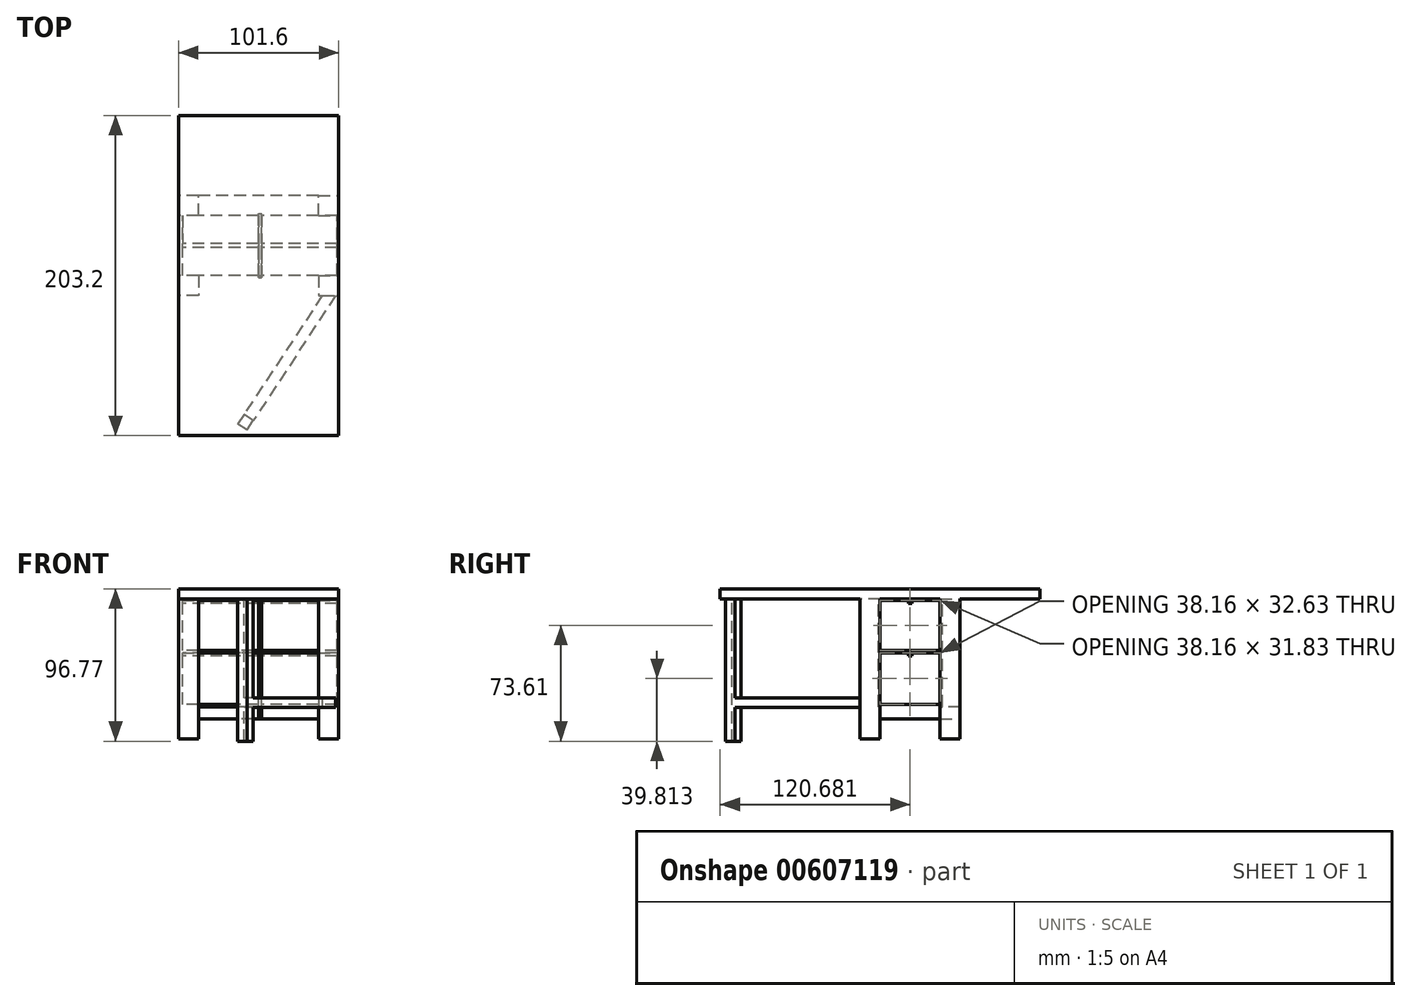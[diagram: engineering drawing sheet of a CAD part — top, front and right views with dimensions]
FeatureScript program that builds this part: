
annotation { "Feature Type Name" : "Feature", "Feature Type Description" : "" }
export const myFeature = defineFeature(function(context is Context, id is Id, definition is map)
    precondition{}
    {
        {
            var Q0;
            Q0=qCreatedBy(makeId("Top.planeOp"),FACE);
            var sketch = newSketch(context, id + "F0", { "sketchPlane" : qUnion([Q0])});
            skLineSegment(sketch, "E0.bottom", {"start": v(-51.6, 50.8) * mm, "end": v(24.6, 50.8) * mm});
            skLineSegment(sketch, "E0.top", {"start": v(-51.6, 12.7) * mm, "end": v(24.6, 12.7) * mm});
            skLineSegment(sketch, "E0.left", {"start": v(-51.6, 50.8) * mm, "end": v(-51.6, 12.7) * mm});
            skLineSegment(sketch, "E0.right", {"start": v(24.6, 50.8) * mm, "end": v(24.6, 12.7) * mm});
            skLineSegment(sketch, "E1.bottom", {"start": v(-51.6, 50.8) * mm, "end": v(-64.3, 50.8) * mm});
            skLineSegment(sketch, "E1.top", {"start": v(-51.6, 63.5) * mm, "end": v(-64.3, 63.5) * mm});
            skLineSegment(sketch, "E1.left", {"start": v(-51.6, 50.8) * mm, "end": v(-51.6, 63.5) * mm});
            skLineSegment(sketch, "E1.right", {"start": v(-64.3, 50.8) * mm, "end": v(-64.3, 63.5) * mm});
            skLineSegment(sketch, "E2.bottom", {"start": v(24.6, 50.8) * mm, "end": v(37.3, 50.8) * mm});
            skLineSegment(sketch, "E2.top", {"start": v(24.6, 63.5) * mm, "end": v(37.3, 63.5) * mm});
            skLineSegment(sketch, "E2.left", {"start": v(24.6, 50.8) * mm, "end": v(24.6, 63.5) * mm});
            skLineSegment(sketch, "E2.right", {"start": v(37.3, 50.8) * mm, "end": v(37.3, 63.5) * mm});
            skLineSegment(sketch, "E3.bottom", {"start": v(24.6, 12.7) * mm, "end": v(37.3, 12.7) * mm});
            skLineSegment(sketch, "E3.top", {"start": v(24.6, 0) * mm, "end": v(37.3, 0) * mm});
            skLineSegment(sketch, "E3.left", {"start": v(24.6, 12.7) * mm, "end": v(24.6, 0) * mm});
            skLineSegment(sketch, "E3.right", {"start": v(37.3, 12.7) * mm, "end": v(37.3, 0) * mm});
            skLineSegment(sketch, "E4.bottom", {"start": v(-51.6, 12.7) * mm, "end": v(-64.3, 12.7) * mm});
            skLineSegment(sketch, "E4.top", {"start": v(-51.6, 0) * mm, "end": v(-64.3, 0) * mm});
            skLineSegment(sketch, "E4.left", {"start": v(-51.6, 12.7) * mm, "end": v(-51.6, 0) * mm});
            skLineSegment(sketch, "E4.right", {"start": v(-64.3, 12.7) * mm, "end": v(-64.3, 0) * mm});
            skLineSegment(sketch, "E5.bottom", {"start": v(-64.3, 50.8) * mm, "end": v(-51.6, 50.8) * mm});
            skLineSegment(sketch, "E5.top", {"start": v(-64.3, 12.7) * mm, "end": v(-51.6, 12.7) * mm});
            skLineSegment(sketch, "E5.left", {"start": v(-64.3, 50.8) * mm, "end": v(-64.3, 12.7) * mm});
            skLineSegment(sketch, "E6.top", {"start": v(-51.6, 0) * mm, "end": v(24.6, 0) * mm});
            skLineSegment(sketch, "E7.right", {"start": v(37.3, 50.8) * mm, "end": v(37.3, 12.7) * mm});
            skLineSegment(sketch, "E8.bottom", {"start": v(24.6, 63.5) * mm, "end": v(-51.6, 63.5) * mm});
            skLineSegment(sketch, "E8.top", {"start": v(24.6, 50.8) * mm, "end": v(-51.6, 50.8) * mm});
            skLineSegment(sketch, "E8.left", {"start": v(24.6, 63.5) * mm, "end": v(24.6, 50.8) * mm});
            skLineSegment(sketch, "E8.right", {"start": v(-51.6, 63.5) * mm, "end": v(-51.6, 50.8) * mm});
            skSolve(sketch);
        }
        {
            var Q0;
            Q0=makeQuery(id+"F0.imprint","IMPRINT",FACE,{"disambiguationData":[TD([[makeQuery(id+"F0.imprint","IMPRINT",EDGE,{"derivedFrom":sQuery(id+"F0.wireOp",EDGE,"E1.top")}),1.0]])]});
            var Q1;
            Q1=makeQuery(id+"F0.imprint","IMPRINT",FACE,{"disambiguationData":[TD([[makeQuery(id+"F0.imprint","IMPRINT",EDGE,{"derivedFrom":sQuery(id+"F0.wireOp",EDGE,"E5.bottom")}),-1.0]])]});
            var Q2;
            Q2=makeQuery(id+"F0.imprint","IMPRINT",FACE,{"disambiguationData":[TD([[makeQuery(id+"F0.imprint","IMPRINT",EDGE,{"derivedFrom":sQuery(id+"F0.wireOp",EDGE,"E4.top")}),-1.0]])]});
            var Q3;
            Q3=makeQuery(id+"F0.imprint","IMPRINT",FACE,{"disambiguationData":[TD([[makeQuery(id+"F0.imprint","IMPRINT",EDGE,{"derivedFrom":sQuery(id+"F0.wireOp",EDGE,"E0.top")}),-1.0]])]});
            var Q4;
            Q4=makeQuery(id+"F0.imprint","IMPRINT",FACE,{"disambiguationData":[TD([[makeQuery(id+"F0.imprint","IMPRINT",EDGE,{"derivedFrom":sQuery(id+"F0.wireOp",EDGE,"E3.top")}),1.0]])]});
            var Q5;
            Q5=makeQuery(id+"F0.imprint","IMPRINT",FACE,{"disambiguationData":[TD([[makeQuery(id+"F0.imprint","IMPRINT",EDGE,{"derivedFrom":sQuery(id+"F0.wireOp",EDGE,"E2.bottom")}),-1.0]])]});
            var Q6;
            Q6=makeQuery(id+"F0.imprint","IMPRINT",FACE,{"disambiguationData":[TD([[makeQuery(id+"F0.imprint","IMPRINT",EDGE,{"derivedFrom":sQuery(id+"F0.wireOp",EDGE,"E2.top")}),-1.0]])]});
            var Q7;
            Q7=makeQuery(id+"F0.imprint","IMPRINT",FACE,{"disambiguationData":[TD([[makeQuery(id+"F0.imprint","IMPRINT",EDGE,{"derivedFrom":sQuery(id+"F0.wireOp",EDGE,"E8.bottom")}),1.0]])]});
            extrude(context, id + "F1", {"entities" : qUnion([Q0, Q1, Q2, Q3, Q4, Q5, Q6, Q7]), "depth" : 7.62 * mm, "offsetDistance" : 25.4 * mm});
        }
        {
            var Q0;
            Q0=makeQuery(id+"F0.imprint","IMPRINT",FACE,{"disambiguationData":[TD([[makeQuery(id+"F0.imprint","IMPRINT",EDGE,{"derivedFrom":sQuery(id+"F0.wireOp",EDGE,"E4.top")}),-1.0]])]});
            var Q1;
            Q1=makeQuery(id+"F0.imprint","IMPRINT",FACE,{"disambiguationData":[TD([[makeQuery(id+"F0.imprint","IMPRINT",EDGE,{"derivedFrom":sQuery(id+"F0.wireOp",EDGE,"E1.top")}),1.0]])]});
            var Q2;
            Q2=makeQuery(id+"F0.imprint","IMPRINT",FACE,{"disambiguationData":[TD([[makeQuery(id+"F0.imprint","IMPRINT",EDGE,{"derivedFrom":sQuery(id+"F0.wireOp",EDGE,"E2.top")}),-1.0]])]});
            var Q3;
            Q3=makeQuery(id+"F0.imprint","IMPRINT",FACE,{"disambiguationData":[TD([[makeQuery(id+"F0.imprint","IMPRINT",EDGE,{"derivedFrom":sQuery(id+"F0.wireOp",EDGE,"E3.top")}),1.0]])]});
            extrude(context, id + "F2", {"entities" : qUnion([Q0, Q1, Q2, Q3]), "operationType" : NewBodyOperationType.ADD, "oppositeDirection" : true, "depth" : 12.7 * mm, "offsetDistance" : 25.4 * mm});
        }
        {
            var Q0;
            Q0=makeQuery(id+"F0.imprint","IMPRINT",FACE,{"disambiguationData":[TD([[makeQuery(id+"F0.imprint","IMPRINT",EDGE,{"derivedFrom":sQuery(id+"F0.wireOp",EDGE,"E3.top")}),1.0]])]});
            var Q1;
            Q1=makeQuery(id+"F0.imprint","IMPRINT",FACE,{"disambiguationData":[TD([[makeQuery(id+"F0.imprint","IMPRINT",EDGE,{"derivedFrom":sQuery(id+"F0.wireOp",EDGE,"E2.top")}),-1.0]])]});
            var Q2;
            Q2=makeQuery(id+"F0.imprint","IMPRINT",FACE,{"disambiguationData":[TD([[makeQuery(id+"F0.imprint","IMPRINT",EDGE,{"derivedFrom":sQuery(id+"F0.wireOp",EDGE,"E1.top")}),1.0]])]});
            var Q3;
            Q3=makeQuery(id+"F0.imprint","IMPRINT",FACE,{"disambiguationData":[TD([[makeQuery(id+"F0.imprint","IMPRINT",EDGE,{"derivedFrom":sQuery(id+"F0.wireOp",EDGE,"E4.top")}),-1.0]])]});
            extrude(context, id + "F3", {"entities" : qUnion([Q0, Q1, Q2, Q3]), "operationType" : NewBodyOperationType.ADD, "depth" : 76.2 * mm, "offsetDistance" : 25.4 * mm});
        }
        {
            var Q0;
            Q0=makeQuery(id+"F3.opExtrude","CAP_FACE",FACE,{"disambiguationData":[OSD([sQuery(id+"F0.wireOp",EDGE,"E1.top"),sQuery(id+"F0.wireOp",EDGE,"E1.right"),sQuery(id+"F0.wireOp",EDGE,"E5.bottom"),sQuery(id+"F0.wireOp",EDGE,"E8.right")])],"isStart":false});
            var sketch = newSketch(context, id + "F4", { "sketchPlane" : qUnion([Q0])});
            skLineSegment(sketch, "E9.top", {"start": v(-64.3, -88.9) * mm, "end": v(37.3, -88.9) * mm});
            skLineSegment(sketch, "E9.left", {"start": v(-64.3, 63.5) * mm, "end": v(-64.3, -88.9) * mm});
            skLineSegment(sketch, "E9.right", {"start": v(37.3, 63.5) * mm, "end": v(37.3, -88.9) * mm});
            skLineSegment(sketch, "E10", {"start": v(37.3, 63.5) * mm, "end": v(37.3, 114.3) * mm});
            skLineSegment(sketch, "E11", {"start": v(-64.3, 63.5) * mm, "end": v(-64.3, 114.3) * mm});
            skLineSegment(sketch, "E12", {"start": v(-64.3, 114.3) * mm, "end": v(37.3, 114.3) * mm});
            skSolve(sketch);
        }
        {
            var Q0;
            Q0 = qSketchRegion(id + "F4", true);
            extrude(context, id + "F5", {"entities" : qUnion([Q0]), "operationType" : NewBodyOperationType.ADD, "depth" : 6.35 * mm, "offsetDistance" : 25.4 * mm});
        }
        {
            var Q0;
            Q0=makeQuery(id+"F5.opExtrude","CAP_FACE",FACE,{"disambiguationData":[OSD([sQuery(id+"F4.wireOp",EDGE,"E9.bottom"),sQuery(id+"F4.wireOp",EDGE,"E9.top"),sQuery(id+"F4.wireOp",EDGE,"E9.left"),sQuery(id+"F4.wireOp",EDGE,"E9.right")])],"isStart":true});
            var sketch = newSketch(context, id + "F6", { "sketchPlane" : qUnion([Q0])});
            skPoint(sketch, "E13.firstSnap0", {"position": v(-13.5, 88.9) * mm});
            skLineSegment(sketch, "E13.bottom", {"start": v(-13.5, -12.7) * mm, "end": v(-11.51, -12.7) * mm});
            skLineSegment(sketch, "E13.top", {"start": v(-13.5, -50.86) * mm, "end": v(-11.51, -50.86) * mm});
            skLineSegment(sketch, "E13.left", {"start": v(-13.5, -12.7) * mm, "end": v(-13.5, -50.86) * mm});
            skLineSegment(sketch, "E13.right", {"start": v(-11.51, -12.7) * mm, "end": v(-11.51, -50.86) * mm});
            skSolve(sketch);
        }
        {
            var Q0;
            Q0 = qSketchRegion(id + "F6", true);
            extrude(context, id + "F7", {"entities" : qUnion([Q0]), "operationType" : NewBodyOperationType.ADD, "depth" : 76.2 * mm, "offsetDistance" : 25.4 * mm});
        }
        {
            var Q0;
            Q0=makeQuery(id+"F7.opExtrude","SWEPT_FACE",FACE,{"disambiguationData":[OSD([sQuery(id+"F6.wireOp",EDGE,"E13.right")])]});
            var sketch = newSketch(context, id + "F8", { "sketchPlane" : qUnion([Q0])});
            skLineSegment(sketch, "E14", {"start": v(12.7, 76.2) * mm, "end": v(12.7, 43.47) * mm});
            skLineSegment(sketch, "E15", {"start": v(12.7, 43.47) * mm, "end": v(50.86, 43.47) * mm});
            skLineSegment(sketch, "E16", {"start": v(50.86, 43.47) * mm, "end": v(50.86, 76.2) * mm});
            skLineSegment(sketch, "E17", {"start": v(50.86, 41.9) * mm, "end": v(33.02, 41.9) * mm});
            skLineSegment(sketch, "E18", {"start": v(12.7, 41.9) * mm, "end": v(30.57, 41.9) * mm});
            skLineSegment(sketch, "E19", {"start": v(30.57, 41.9) * mm, "end": v(30.57, 39.96) * mm});
            skLineSegment(sketch, "E20", {"start": v(30.57, 39.96) * mm, "end": v(33.02, 39.96) * mm});
            skLineSegment(sketch, "E21", {"start": v(33.02, 39.96) * mm, "end": v(33.02, 41.9) * mm});
            skLineSegment(sketch, "E22", {"start": v(12.7, 41.9) * mm, "end": v(12.7, 9.28) * mm});
            skLineSegment(sketch, "E23", {"start": v(50.86, 41.9) * mm, "end": v(50.86, 9.28) * mm});
            skLineSegment(sketch, "E24", {"start": v(12.7, 9.28) * mm, "end": v(50.86, 9.28) * mm});
            skLineSegment(sketch, "E25", {"start": v(50.86, 75.3) * mm, "end": v(33.02, 75.3) * mm});
            skLineSegment(sketch, "E26", {"start": v(12.7, 75.3) * mm, "end": v(30.57, 75.3) * mm});
            skLineSegment(sketch, "E27", {"start": v(30.57, 75.3) * mm, "end": v(30.57, 73.52) * mm});
            skLineSegment(sketch, "E28", {"start": v(30.57, 73.52) * mm, "end": v(33.02, 73.52) * mm});
            skLineSegment(sketch, "E29", {"start": v(33.02, 73.52) * mm, "end": v(33.02, 75.3) * mm});
            skSolve(sketch);
        }
        {
            var Q0;
            Q0=makeQuery(id+"F8.imprint","IMPRINT",FACE,{"disambiguationData":[TD([[makeQuery(id+"F8.imprint","IMPRINT",EDGE,{"derivedFrom":sQuery(id+"F8.wireOp",EDGE,"E17")}),1.0]])]});
            extrude(context, id + "F9", {"entities" : qUnion([Q0]), "operationType" : NewBodyOperationType.ADD, "depth" : 47.75 * mm, "offsetDistance" : 25.4 * mm, "hasSecondDirection" : true, "secondDirectionOppositeDirection" : true, "secondDirectionDepth" : 50.3 * mm});
        }
        {
            var Q0;
            {var subQ1=sQuery(id+"F8.wireOp",EDGE,"E15");Q0=makeQuery(id+"F8.imprint","IMPRINT",FACE,{"disambiguationData":[TD([[makeQuery(id+"F8.imprint","IMPRINT",EDGE,{"derivedFrom":subQ1}),1.0]])]});}
            extrude(context, id + "F10", {"entities" : qUnion([Q0]), "operationType" : NewBodyOperationType.ADD, "depth" : 47.75 * mm, "offsetDistance" : 25.4 * mm, "hasSecondDirection" : true, "secondDirectionOppositeDirection" : true, "secondDirectionDepth" : 50.3 * mm});
        }
        {
            var Q0;
            Q0=makeQuery(id+"F10.boolean.opBoolean","MERGE",FACE,{"derivedFrom":[makeQuery(id+"F9.boolean.opBoolean","MERGE",FACE,{"derivedFrom":[makeQuery(id+"F7.opExtrude","SWEPT_FACE",FACE,{"disambiguationData":[OSD([sQuery(id+"F6.wireOp",EDGE,"E13.top")])]}),makeQuery(id+"F9.opExtrude","SWEPT_FACE",FACE,{"disambiguationData":[OSD([sQuery(id+"F8.wireOp",EDGE,"E23")])]})]}),makeQuery(id+"F10.opExtrude","SWEPT_FACE",FACE,{"disambiguationData":[OSD([sQuery(id+"F8.wireOp",EDGE,"E16")])]})]});
            var sketch = newSketch(context, id + "F11", { "sketchPlane" : qUnion([Q0])});
            skLineSegment(sketch, "E30.bottom", {"start": v(11.51, 76.2) * mm, "end": v(13.5, 76.2) * mm});
            skLineSegment(sketch, "E30.top", {"start": v(11.51, 7.62) * mm, "end": v(13.5, 7.62) * mm});
            skLineSegment(sketch, "E30.left", {"start": v(11.51, 76.2) * mm, "end": v(11.51, 7.62) * mm});
            skLineSegment(sketch, "E30.right", {"start": v(13.5, 76.2) * mm, "end": v(13.5, 7.62) * mm});
            skSolve(sketch);
        }
        {
            var Q0;
            Q0 = qSketchRegion(id + "F11", true);
            extrude(context, id + "F12", {"entities" : qUnion([Q0]), "operationType" : NewBodyOperationType.ADD, "depth" : 1.27 * mm, "offsetDistance" : 25.4 * mm, "hasSecondDirection" : true, "secondDirectionOppositeDirection" : true, "secondDirectionDepth" : 39.37 * mm});
        }
        {
            var Q0;
            Q0=makeQuery(id+"F5.opExtrude","CAP_FACE",FACE,{"disambiguationData":[OSD([sQuery(id+"F4.wireOp",EDGE,"E9.bottom"),sQuery(id+"F4.wireOp",EDGE,"E9.top"),sQuery(id+"F4.wireOp",EDGE,"E9.left"),sQuery(id+"F4.wireOp",EDGE,"E9.right")])],"isStart":true});
            var sketch = newSketch(context, id + "F13", { "sketchPlane" : qUnion([Q0])});
            skPoint(sketch, "E31.startSnap0", {"position": v(-13.5, 88.9) * mm});
            skPoint(sketch, "E32.endSnap0", {"position": v(30.96, 0) * mm});
            skLineSegment(sketch, "E33", {"start": v(-20.8, 85.47) * mm, "end": v(-26.73, 81.56) * mm});
            skLineSegment(sketch, "E34", {"start": v(-20.8, 85.47) * mm, "end": v(-16.88, 79.53) * mm});
            skLineSegment(sketch, "E35", {"start": v(-16.88, 79.53) * mm, "end": v(-22.82, 75.62) * mm});
            skLineSegment(sketch, "E36", {"start": v(-22.82, 75.62) * mm, "end": v(-26.73, 81.56) * mm});
            skSolve(sketch);
        }
        {
            var Q0;
            Q0 = qSketchRegion(id + "F13", true);
            extrude(context, id + "F14", {"entities" : qUnion([Q0]), "operationType" : NewBodyOperationType.ADD, "depth" : 90.17 * mm, "offsetDistance" : 25.4 * mm});
        }
        {
            var Q0;
            Q0 = qSketchRegion(id + "F13", true);
            extrude(context, id + "F15", {"entities" : qUnion([Q0]), "operationType" : NewBodyOperationType.ADD, "depth" : 90.42 * mm, "offsetDistance" : 25.4 * mm});
        }
        {
            var Q0;
            {var subQ0=sQuery(id+"F13.wireOp",EDGE,"E35");Q0=makeQuery(id+"F15.boolean.opBoolean","MERGE",FACE,{"derivedFrom":[makeQuery(id+"F14.opExtrude","SWEPT_FACE",FACE,{"disambiguationData":[OSD([subQ0])]}),makeQuery(id+"F15.opExtrude","SWEPT_FACE",FACE,{"disambiguationData":[OSD([subQ0])]})]});}
            var sketch = newSketch(context, id + "F16", { "sketchPlane" : qUnion([Q0])});
            skLineSegment(sketch, "E37.bottom", {"start": v(-29.66, 13.33) * mm, "end": v(-22.55, 13.33) * mm});
            skLineSegment(sketch, "E37.top", {"start": v(-29.66, 7.29) * mm, "end": v(-22.55, 7.29) * mm});
            skLineSegment(sketch, "E37.left", {"start": v(-29.66, 13.33) * mm, "end": v(-29.66, 7.29) * mm});
            skLineSegment(sketch, "E37.right", {"start": v(-22.55, 13.33) * mm, "end": v(-22.55, 7.29) * mm});
            skSolve(sketch);
        }
        {
            var Q0;
            Q0 = qSketchRegion(id + "F16", true);
            extrude(context, id + "F17", {"entities" : qUnion([Q0]), "operationType" : NewBodyOperationType.ADD, "depth" : 97.03 * mm, "offsetDistance" : 25.4 * mm});
        }
    });
